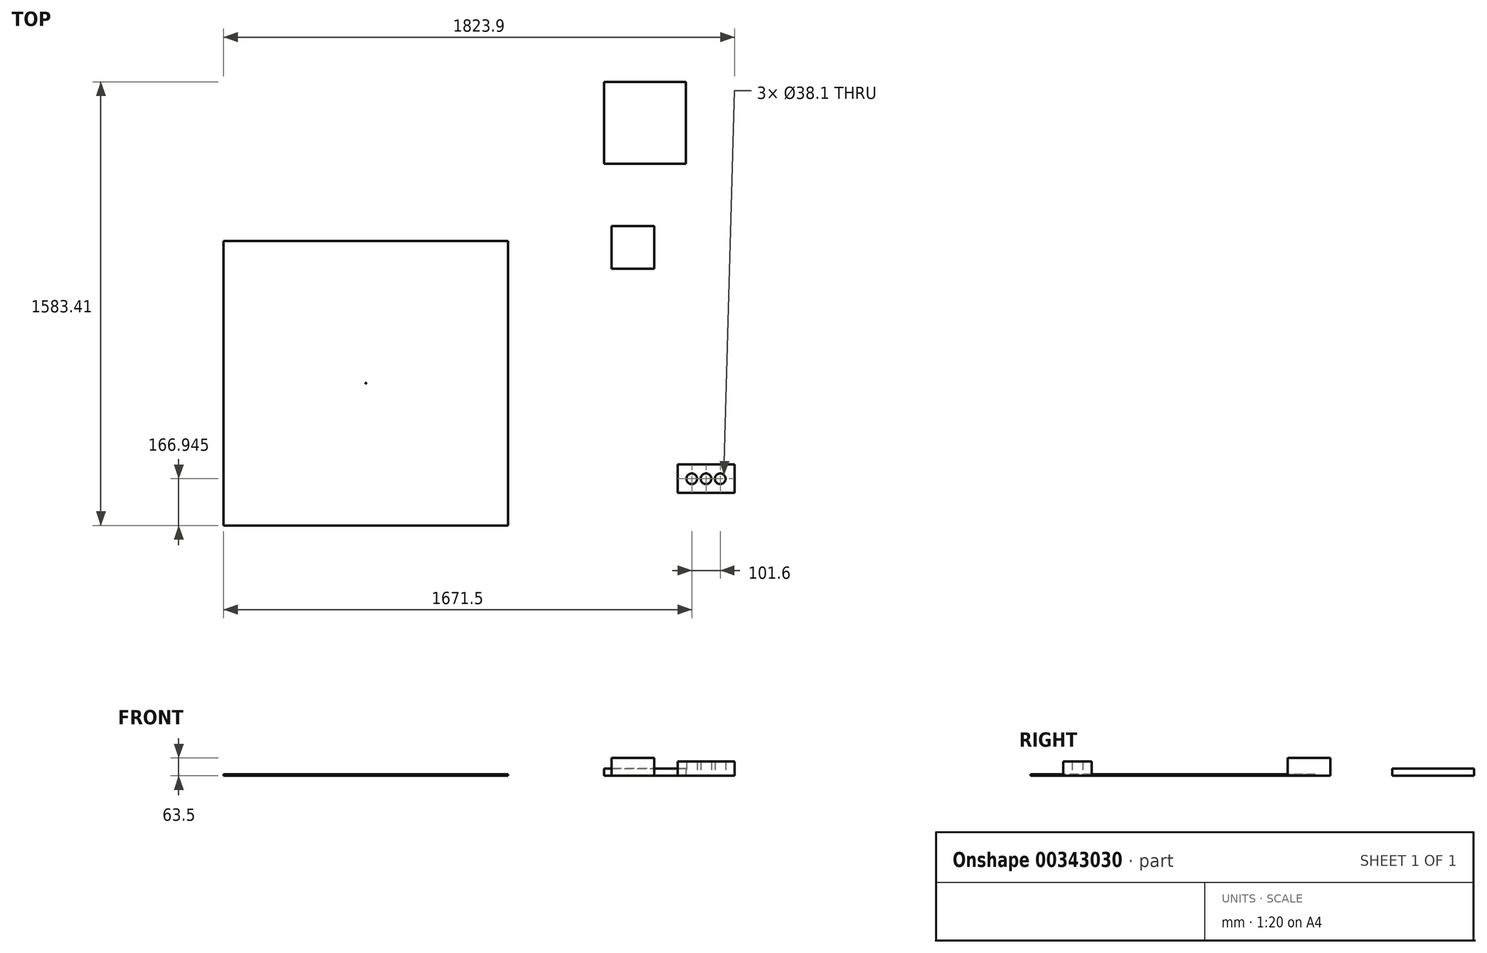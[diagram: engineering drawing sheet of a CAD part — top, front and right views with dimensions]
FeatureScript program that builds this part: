
annotation { "Feature Type Name" : "Feature", "Feature Type Description" : "" }
export const myFeature = defineFeature(function(context is Context, id is Id, definition is map)
    precondition{}
    {
        {
            var Q0;
            Q0=qCreatedBy(makeId("Top.planeOp"),FACE);
            var sketch = newSketch(context, id + "F0", { "sketchPlane" : qUnion([Q0])});
            skLineSegment(sketch, "E0", {"start": v(723.55, 120.63) * mm, "end": v(-292.45, 120.63) * mm});
            skLineSegment(sketch, "E1", {"start": v(-292.45, 120.63) * mm, "end": v(-292.45, 1136.63) * mm});
            skLineSegment(sketch, "E2", {"start": v(-292.45, 1136.63) * mm, "end": v(723.55, 1136.63) * mm});
            skLineSegment(sketch, "E3", {"start": v(723.55, 1136.63) * mm, "end": v(723.55, 120.63) * mm});
            skLineSegment(sketch, "E4", {"start": v(1092.02, 1190.35) * mm, "end": v(1092.02, 1037.95) * mm});
            skLineSegment(sketch, "E5", {"start": v(1092.02, 1037.95) * mm, "end": v(1244.42, 1037.95) * mm});
            skLineSegment(sketch, "E6", {"start": v(1244.42, 1037.95) * mm, "end": v(1244.42, 1190.35) * mm});
            skLineSegment(sketch, "E7", {"start": v(1244.42, 1190.35) * mm, "end": v(1092.02, 1190.35) * mm});
            skLineSegment(sketch, "E8", {"start": v(1065.58, 1704.04) * mm, "end": v(1065.58, 1411.94) * mm});
            skLineSegment(sketch, "E9", {"start": v(1065.58, 1411.94) * mm, "end": v(1357.68, 1411.94) * mm});
            skLineSegment(sketch, "E10", {"start": v(1357.68, 1411.94) * mm, "end": v(1357.68, 1704.04) * mm});
            skLineSegment(sketch, "E11", {"start": v(1357.68, 1704.04) * mm, "end": v(1065.58, 1704.04) * mm});
            skCircle(sketch, "E12", {"center": v(215.55, 628.63) * mm, "radius": 1.27 * mm});
            skSolve(sketch);
        }
        {
            var Q0;
            Q0=makeQuery(id+"F0.imprint","IMPRINT",FACE,{"disambiguationData":[TD([[makeQuery(id+"F0.imprint","IMPRINT",EDGE,{"derivedFrom":sQuery(id+"F0.wireOp",EDGE,"E8")}),1.0]])]});
            extrude(context, id + "F1", {"entities" : qUnion([Q0]), "depth" : 25.4 * mm});
        }
        {
            var Q0;
            Q0=makeQuery(id+"F0.imprint","IMPRINT",FACE,{"disambiguationData":[TD([[makeQuery(id+"F0.imprint","IMPRINT",EDGE,{"derivedFrom":sQuery(id+"F0.wireOp",EDGE,"E4")}),1.0]])]});
            extrude(context, id + "F2", {"entities" : qUnion([Q0]), "depth" : 63.5 * mm});
        }
        {
            var Q0;
            Q0=makeQuery(id+"F0.imprint","IMPRINT",FACE,{"disambiguationData":[TD([[makeQuery(id+"F0.imprint","IMPRINT",EDGE,{"derivedFrom":sQuery(id+"F0.wireOp",EDGE,"E0")}),-1.0]])]});
            extrude(context, id + "F3", {"entities" : qUnion([Q0]), "depth" : 5.08 * mm});
        }
        {
            var Q0;
            Q0=qCreatedBy(makeId("Top.planeOp"),FACE);
            var sketch = newSketch(context, id + "F4", { "sketchPlane" : qUnion([Q0])});
            skLineSegment(sketch, "E13", {"start": v(1328.25, 338.38) * mm, "end": v(1328.25, 236.78) * mm});
            skLineSegment(sketch, "E14", {"start": v(1328.25, 236.78) * mm, "end": v(1531.45, 236.78) * mm});
            skLineSegment(sketch, "E15", {"start": v(1531.45, 236.78) * mm, "end": v(1531.45, 338.38) * mm});
            skLineSegment(sketch, "E16", {"start": v(1531.45, 338.38) * mm, "end": v(1328.25, 338.38) * mm});
            skCircle(sketch, "E17", {"center": v(1429.85, 287.58) * mm, "radius": 19.05 * mm});
            skCircle(sketch, "E18", {"center": v(1480.65, 287.58) * mm, "radius": 19.05 * mm});
            skCircle(sketch, "E19", {"center": v(1379.05, 287.58) * mm, "radius": 19.05 * mm});
            skSolve(sketch);
        }
        {
            var Q0;
            Q0=makeQuery(id+"F4.imprint","IMPRINT",FACE,{"disambiguationData":[TD([[makeQuery(id+"F4.imprint","IMPRINT",EDGE,{"derivedFrom":sQuery(id+"F4.wireOp",EDGE,"E13")}),1.0]])]});
            extrude(context, id + "F5", {"entities" : qUnion([Q0]), "depth" : 50.8 * mm});
        }
    });
